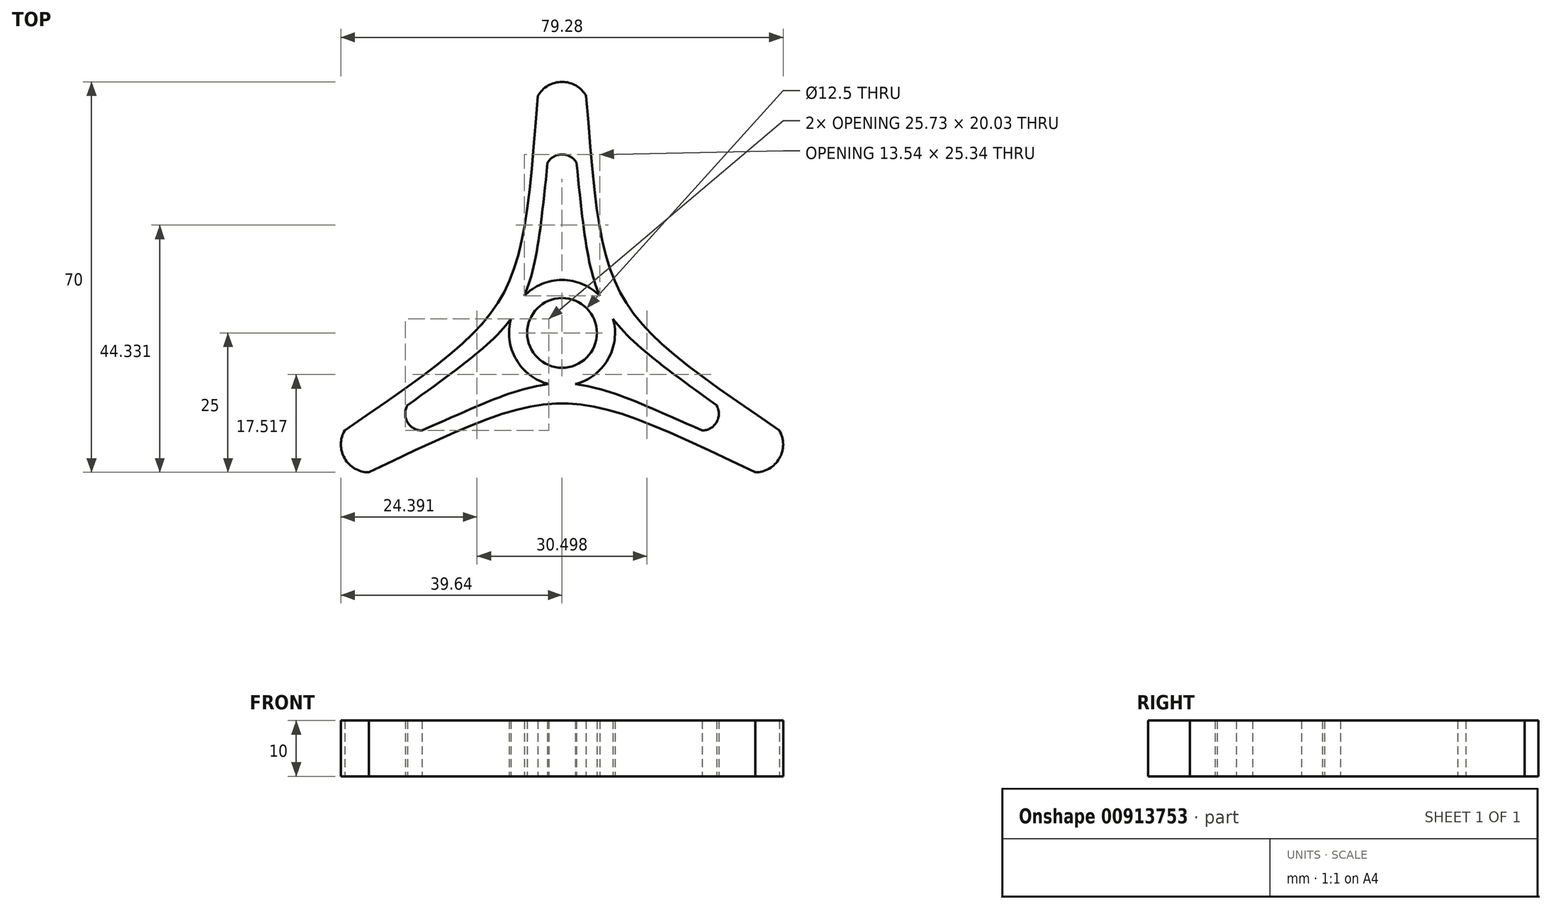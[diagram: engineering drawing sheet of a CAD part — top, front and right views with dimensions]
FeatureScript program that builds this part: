
annotation { "Feature Type Name" : "Feature", "Feature Type Description" : "" }
export const myFeature = defineFeature(function(context is Context, id is Id, definition is map)
    precondition{}
    {
        {
            var Q0;
            Q0=qCreatedBy(makeId("Top.planeOp"),FACE);
            var sketch = newSketch(context, id + "F0", { "sketchPlane" : qUnion([Q0])});
            skCircle(sketch, "E0", {"center": v(0, 0) * mm, "radius": 9.5 * mm});
            skCircle(sketch, "E1", {"center": v(0, 0) * mm, "radius": 6.25 * mm});
            skPoint(sketch, "E2.cCircle.perimeterSnap0", {"position": v(0, 5.25) * mm});
            skPoint(sketch, "E2.0.startSnap0", {"position": v(0, 5.25) * mm});
            skPoint(sketch, "E3.visualSharp", {"position": v(0, 50) * mm});
            skArc(sketch, "E3.filletArc", {"start": v(4.33, 42.5) * mm, "mid": v(0, 45) * mm, "end": v(-4.33, 42.5) * mm});
            skPoint(sketch, "E4.visualSharp", {"position": v(43.3, -25) * mm});
            skArc(sketch, "E4.filletArc", {"start": v(34.64, -25) * mm, "mid": v(38.97, -22.5) * mm, "end": v(38.97, -17.5) * mm});
            skPoint(sketch, "E5.visualSharp", {"position": v(-43.3, -25) * mm});
            skArc(sketch, "E5.filletArc", {"start": v(-38.97, -17.5) * mm, "mid": v(-38.97, -22.5) * mm, "end": v(-34.64, -25) * mm});
            skPoint(sketch, "E6.visualSharp", {"position": v(0, 35) * mm});
            skArc(sketch, "E6.filletArc", {"start": v(2.6, 30.5) * mm, "mid": v(0, 32) * mm, "end": v(-2.6, 30.5) * mm});
            skPoint(sketch, "E7.visualSharp", {"position": v(30.31, -17.5) * mm});
            skArc(sketch, "E7.filletArc", {"start": v(25.11, -17.5) * mm, "mid": v(27.71, -16) * mm, "end": v(27.71, -13) * mm});
            skPoint(sketch, "E8.visualSharp", {"position": v(-30.31, -17.5) * mm});
            skArc(sketch, "E8.filletArc", {"start": v(-27.71, -13) * mm, "mid": v(-27.71, -16) * mm, "end": v(-25.11, -17.5) * mm});
            skFitSpline(sketch, "E9", {"points": [v(2.6, 30.5) * mm, v(27.71, -13) * mm], "startDerivative": vector(8.44, -82.12) * mm, "endDerivative": vector(66.9, -48.38) * mm});
            skFitSpline(sketch, "E10", {"points": [v(4.33, 42.5) * mm, v(38.97, -17.5) * mm], "startDerivative": vector(9.1, -114.75) * mm, "endDerivative": vector(94.83, -65.25) * mm});
            skFitSpline(sketch, "E11", {"points": [v(25.11, -17.5) * mm, v(-25.11, -17.5) * mm], "startDerivative": vector(-75.34, 33.75) * mm, "endDerivative": vector(-75.34, -33.75) * mm});
            skFitSpline(sketch, "E12", {"points": [v(-34.64, -25) * mm, v(34.64, -25) * mm], "startDerivative": vector(103.92, 49.5) * mm, "endDerivative": vector(103.92, -49.5) * mm});
            skFitSpline(sketch, "E13", {"points": [v(-38.97, -17.5) * mm, v(-4.33, 42.5) * mm], "startDerivative": vector(94.83, 65.25) * mm, "endDerivative": vector(9.1, 114.75) * mm});
            skFitSpline(sketch, "E14", {"points": [v(-2.6, 30.5) * mm, v(-27.71, -13) * mm], "startDerivative": vector(-8.44, -82.13) * mm, "endDerivative": vector(-66.9, -48.37) * mm});
            skSolve(sketch);
        }
        {
            var Q0;
            Q0=makeQuery(id+"F0.imprint","IMPRINT",FACE,{"disambiguationData":[TD([[makeQuery(id+"F0.imprint","IMPRINT",EDGE,{"derivedFrom":sQuery(id+"F0.wireOp",EDGE,"E3.filletArc")}),1.0]])]});
            var Q1;
            {var subQ7=sQuery(id+"F0.wireOp",EDGE,"E0");var subQ13=sQuery(id+"F0.wireOp",EDGE,"E9");var subQ14=makeQuery(id+"F0.imprint","INTERSECT",VERTEX,{"disambiguationData":[OD(0.0)],"derivedFrom":[subQ7,subQ13]});Q1=makeQuery(id+"F0.imprint","IMPRINT",FACE,{"disambiguationData":[TD([[makeQuery(id+"F0.imprint","IMPRINT",EDGE,{"disambiguationData":[TD([[subQ14,-1.0]])],"derivedFrom":subQ7}),1.0]])]});}
            var Q2;
            {var subQ2=sQuery(id+"F0.wireOp",EDGE,"0483c41c-36ec-4fac-bc6d-33c64d23a2b0.0");var subQ4=sQuery(id+"F0.wireOp",EDGE,"0483c41c-36ec-4fac-bc6d-33c64d23a2b0.2");var subQ6=makeQuery(id+"F0.imprint","INTERSECT",VERTEX,{"derivedFrom":[subQ2,subQ4]});Q2=makeQuery(id+"F0.imprint","IMPRINT",FACE,{"disambiguationData":[TD([[makeQuery(id+"F0.imprint","IMPRINT",EDGE,{"disambiguationData":[TD([[subQ6,-1.0]])],"derivedFrom":subQ2}),-1.0]])]});}
            var Q3;
            {var subQ0=sQuery(id+"F0.wireOp",EDGE,"E11");var subQ1=sQuery(id+"F0.wireOp",EDGE,"E0");var subQ2=makeQuery(id+"F0.imprint","INTERSECT",VERTEX,{"disambiguationData":[OD(0.0)],"derivedFrom":[subQ1,subQ0]});Q3=makeQuery(id+"F0.imprint","IMPRINT",FACE,{"disambiguationData":[TD([[makeQuery(id+"F0.imprint","IMPRINT",EDGE,{"disambiguationData":[TD([[subQ2,-1.0]])],"derivedFrom":subQ1}),1.0]])]});}
            var Q4;
            {var subQ2=sQuery(id+"F0.wireOp",EDGE,"0483c41c-36ec-4fac-bc6d-33c64d23a2b0.2");var subQ4=sQuery(id+"F0.wireOp",EDGE,"0483c41c-36ec-4fac-bc6d-33c64d23a2b0.1");var subQ6=makeQuery(id+"F0.imprint","INTERSECT",VERTEX,{"derivedFrom":[subQ4,subQ2]});Q4=makeQuery(id+"F0.imprint","IMPRINT",FACE,{"disambiguationData":[TD([[makeQuery(id+"F0.imprint","IMPRINT",EDGE,{"disambiguationData":[TD([[subQ6,1.0]])],"derivedFrom":subQ4}),-1.0]])]});}
            var Q5;
            {var subQ2=sQuery(id+"F0.wireOp",EDGE,"0483c41c-36ec-4fac-bc6d-33c64d23a2b0.1");var subQ4=sQuery(id+"F0.wireOp",EDGE,"0483c41c-36ec-4fac-bc6d-33c64d23a2b0.0");var subQ6=makeQuery(id+"F0.imprint","INTERSECT",VERTEX,{"derivedFrom":[subQ4,subQ2]});Q5=makeQuery(id+"F0.imprint","IMPRINT",FACE,{"disambiguationData":[TD([[makeQuery(id+"F0.imprint","IMPRINT",EDGE,{"disambiguationData":[TD([[subQ6,1.0]])],"derivedFrom":subQ4}),-1.0]])]});}
            var Q6;
            {var subQ0=sQuery(id+"F0.wireOp",EDGE,"E14");var subQ1=sQuery(id+"F0.wireOp",EDGE,"E0");var subQ2=makeQuery(id+"F0.imprint","INTERSECT",VERTEX,{"disambiguationData":[OD(0.0)],"derivedFrom":[subQ1,subQ0]});Q6=makeQuery(id+"F0.imprint","IMPRINT",FACE,{"disambiguationData":[TD([[makeQuery(id+"F0.imprint","IMPRINT",EDGE,{"disambiguationData":[TD([[subQ2,-1.0]])],"derivedFrom":subQ1}),1.0]])]});}
            var Q7;
            {var subQ0=sQuery(id+"F0.wireOp",EDGE,"E9");var subQ1=sQuery(id+"F0.wireOp",EDGE,"E0");var subQ2=makeQuery(id+"F0.imprint","INTERSECT",VERTEX,{"disambiguationData":[OD(0.0)],"derivedFrom":[subQ1,subQ0]});Q7=makeQuery(id+"F0.imprint","IMPRINT",FACE,{"disambiguationData":[TD([[makeQuery(id+"F0.imprint","IMPRINT",EDGE,{"disambiguationData":[TD([[subQ2,1.0]])],"derivedFrom":subQ1}),1.0]])]});}
            extrude(context, id + "F1", {"entities" : qUnion([Q0, Q1, Q2, Q3, Q4, Q5, Q6, Q7]), "depth" : 10 * mm, "offsetDistance" : 25 * mm});
        }
    });
